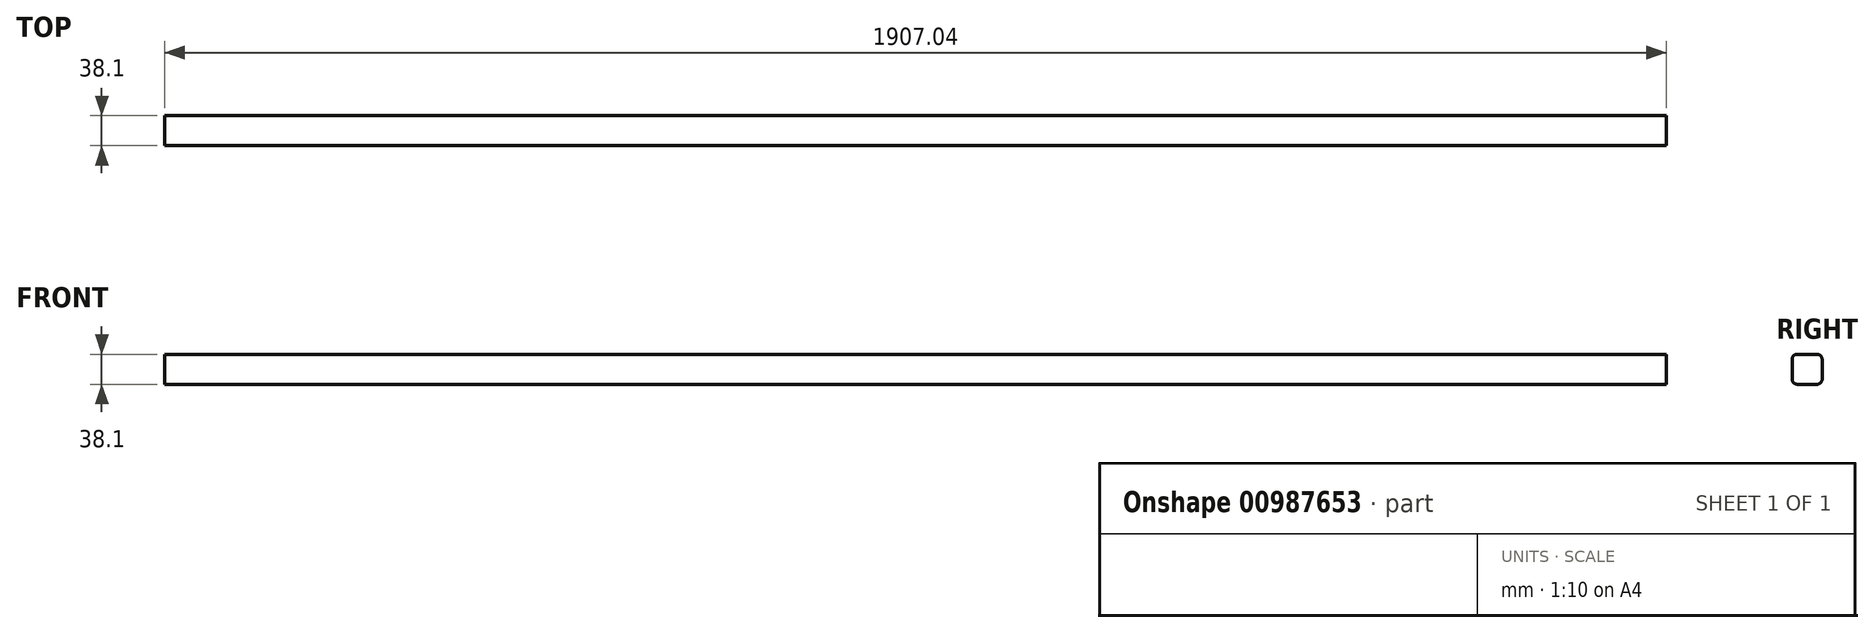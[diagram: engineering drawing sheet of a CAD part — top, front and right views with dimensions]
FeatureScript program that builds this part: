
annotation { "Feature Type Name" : "Feature", "Feature Type Description" : "" }
export const myFeature = defineFeature(function(context is Context, id is Id, definition is map)
    precondition{}
    {
        {
            var Q0;
            Q0=qCreatedBy(makeId("Right.planeOp"),FACE);
            var sketch = newSketch(context, id + "F0", { "sketchPlane" : qUnion([Q0])});
            skLineSegment(sketch, "E0.bottom", {"start": v(19.05, 19.05) * mm, "end": v(-19.05, 19.05) * mm});
            skLineSegment(sketch, "E0.top", {"start": v(19.05, -19.05) * mm, "end": v(-19.05, -19.05) * mm});
            skLineSegment(sketch, "E0.left", {"start": v(19.05, 19.05) * mm, "end": v(19.05, -19.05) * mm});
            skLineSegment(sketch, "E0.right", {"start": v(-19.05, 19.05) * mm, "end": v(-19.05, -19.05) * mm});
            skPoint(sketch, "E0.middle", {"position": v(0, 0) * mm});
            skSolve(sketch);
        }
        {
            var Q0;
            Q0 = qSketchRegion(id + "F0", true);
            extrude(context, id + "F1", {"entities" : qUnion([Q0]), "endBound" : BoundingType.SYMMETRIC, "depth" : 1907.03 * mm, "offsetDistance" : 25.4 * mm});
        }
        {
            var Q0;
            Q0=makeQuery(id+"F1.opExtrude","SWEPT_EDGE",EDGE,{"disambiguationData":[OSD([sQuery(id+"F0.wireOp",EDGE,"E0.bottom"),sQuery(id+"F0.wireOp",EDGE,"E0.right")])]});
            var Q1;
            Q1=makeQuery(id+"F1.opExtrude","SWEPT_EDGE",EDGE,{"disambiguationData":[OSD([sQuery(id+"F0.wireOp",EDGE,"E0.bottom"),sQuery(id+"F0.wireOp",EDGE,"E0.left")])]});
            var Q2;
            Q2=makeQuery(id+"F1.opExtrude","SWEPT_EDGE",EDGE,{"disambiguationData":[OSD([sQuery(id+"F0.wireOp",EDGE,"E0.top"),sQuery(id+"F0.wireOp",EDGE,"E0.left")])]});
            var Q3;
            Q3=makeQuery(id+"F1.opExtrude","SWEPT_EDGE",EDGE,{"disambiguationData":[OSD([sQuery(id+"F0.wireOp",EDGE,"E0.top"),sQuery(id+"F0.wireOp",EDGE,"E0.right")])]});
            fillet(context, id + "F2", {"entities" : qUnion([Q0, Q1, Q2, Q3]), "radius" : 6.35 * mm, "tangentPropagation" : true, "allowEdgeOverflow" : false});
        }
    });
